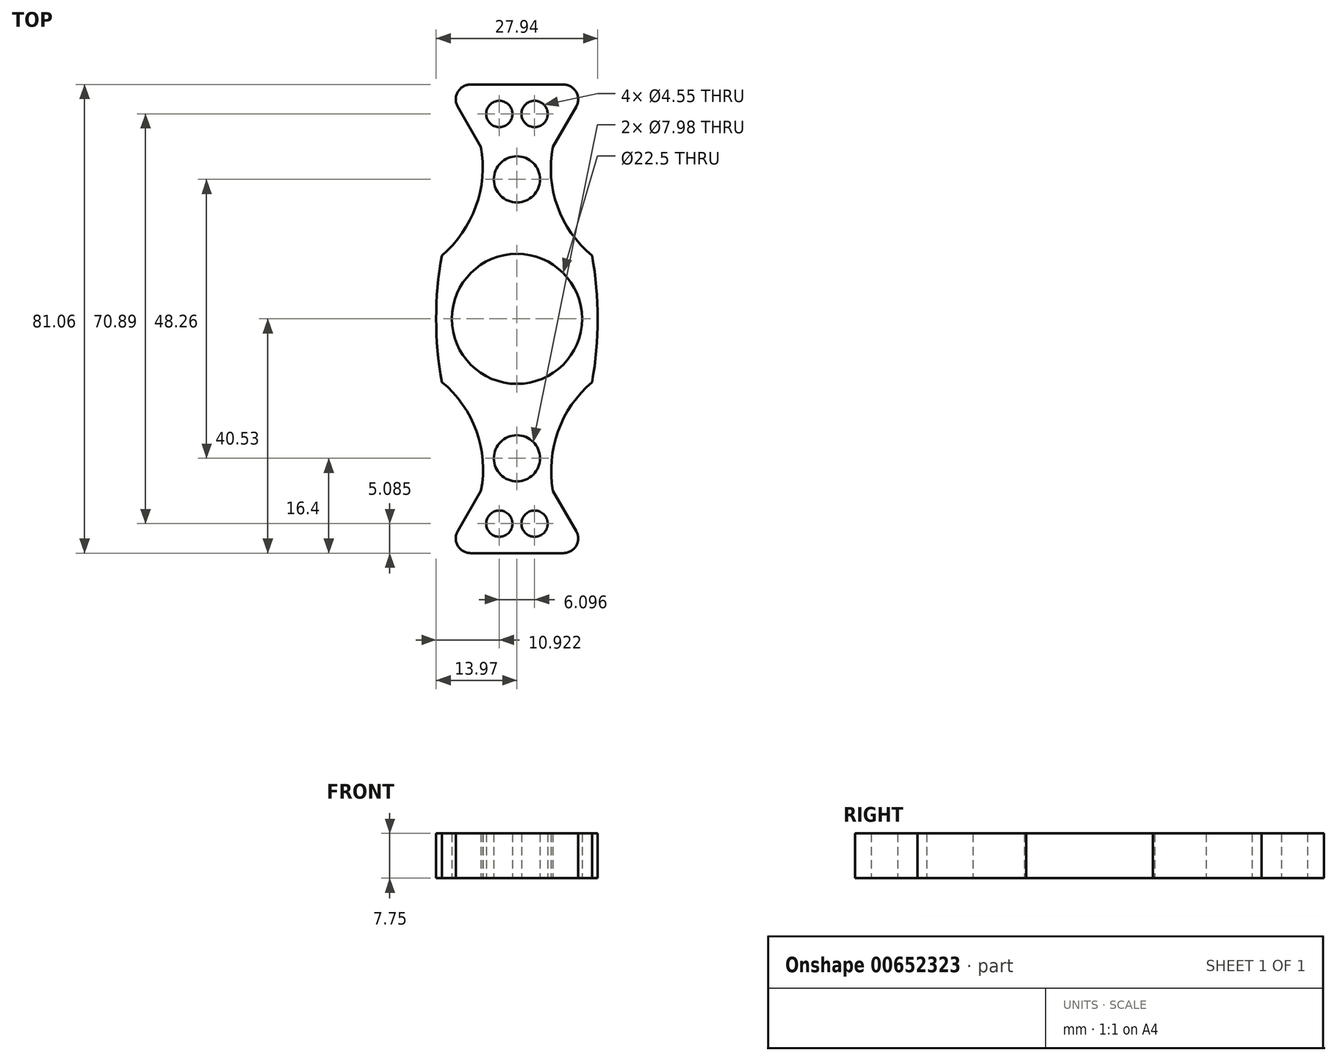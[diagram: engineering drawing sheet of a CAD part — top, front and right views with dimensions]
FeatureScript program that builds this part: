
annotation { "Feature Type Name" : "Feature", "Feature Type Description" : "" }
export const myFeature = defineFeature(function(context is Context, id is Id, definition is map)
    precondition{}
    {
        {
            var Q0;
            Q0=qCreatedBy(makeId("Top.planeOp"),FACE);
            var sketch = newSketch(context, id + "F0", { "sketchPlane" : qUnion([Q0])});
            skCircle(sketch, "E0", {"center": v(0, 0) * mm, "radius": 11.25 * mm});
            skLineSegment(sketch, "E1.0", {"start": v(-6.22, 29.76) * mm, "end": v(-10.24, 36.72) * mm});
            skLineSegment(sketch, "E1.1", {"start": v(-8.04, 40.53) * mm, "end": v(8.04, 40.53) * mm});
            skLineSegment(sketch, "E1.2", {"start": v(10.24, 36.72) * mm, "end": v(6.22, 29.76) * mm});
            skPoint(sketch, "E1.0.midPoint", {"position": v(-6.22, 29.76) * mm});
            skPoint(sketch, "E2.visualSharp", {"position": v(-12.44, 40.53) * mm});
            skArc(sketch, "E2.filletArc", {"start": v(-8.04, 40.53) * mm, "mid": v(-10.24, 39.26) * mm, "end": v(-10.24, 36.72) * mm});
            skPoint(sketch, "E3.visualSharp", {"position": v(12.44, 40.53) * mm});
            skArc(sketch, "E3.filletArc", {"start": v(10.24, 36.72) * mm, "mid": v(10.24, 39.26) * mm, "end": v(8.04, 40.53) * mm});
            skPoint(sketch, "E4.orphan", {"position": v(0, 18.99) * mm});
            skCircle(sketch, "E5", {"center": v(3.05, 35.45) * mm, "radius": 2.27 * mm});
            skCircle(sketch, "E6", {"center": v(-3.05, 35.45) * mm, "radius": 2.27 * mm});
            skLineSegment(sketch, "E7.1.1", {"start": v(-10.24, -36.72) * mm, "end": v(-6.22, -29.76) * mm});
            skArc(sketch, "E7.1.2", {"start": v(-10.24, -36.72) * mm, "mid": v(-10.24, -39.26) * mm, "end": v(-8.04, -40.53) * mm});
            skLineSegment(sketch, "E7.1.3", {"start": v(8.04, -40.53) * mm, "end": v(-8.04, -40.53) * mm});
            skArc(sketch, "E7.1.4", {"start": v(8.04, -40.53) * mm, "mid": v(10.24, -39.26) * mm, "end": v(10.24, -36.72) * mm});
            skLineSegment(sketch, "E7.1.5", {"start": v(6.22, -29.76) * mm, "end": v(10.24, -36.72) * mm});
            skCircle(sketch, "E7.1.10", {"center": v(-3.05, -35.45) * mm, "radius": 2.27 * mm});
            skCircle(sketch, "E7.1.11", {"center": v(3.05, -35.45) * mm, "radius": 2.27 * mm});
            skPoint(sketch, "E8.center.orphan", {"position": v(0, 16.59) * mm});
            skPoint(sketch, "E9.end.orphan", {"position": v(8.58, 10.94) * mm});
            skPoint(sketch, "E10.start.orphan", {"position": v(-8.58, 10.94) * mm});
            skArc(sketch, "E11", {"start": v(-12.98, 10.94) * mm, "mid": v(-13.97, 0) * mm, "end": v(-12.98, -10.94) * mm});
            skArc(sketch, "E12.1.0", {"start": v(12.98, -10.94) * mm, "mid": v(13.97, 0) * mm, "end": v(12.98, 10.94) * mm});
            skArc(sketch, "E13", {"start": v(6.22, 29.76) * mm, "mid": v(7, 19.42) * mm, "end": v(12.98, 10.94) * mm});
            skArc(sketch, "E14", {"start": v(-12.98, 10.94) * mm, "mid": v(-7.1, 19.45) * mm, "end": v(-6.22, 29.76) * mm});
            skArc(sketch, "E15.1.0", {"start": v(12.98, -10.94) * mm, "mid": v(7.1, -19.45) * mm, "end": v(6.22, -29.76) * mm});
            skArc(sketch, "E15.1.1", {"start": v(-6.22, -29.76) * mm, "mid": v(-7, -19.42) * mm, "end": v(-12.98, -10.94) * mm});
            skPoint(sketch, "E16.orphan", {"position": v(6.22, 29.76) * mm});
            skPoint(sketch, "E17.orphan", {"position": v(6.22, -29.76) * mm});
            skPoint(sketch, "E18.center.orphan", {"position": v(0, 29.84) * mm});
            skPoint(sketch, "E1.cCircle.center.orphan", {"position": v(0, 33.35) * mm});
            skPoint(sketch, "E19.center.orphan", {"position": v(0, 24.13) * mm});
            skCircle(sketch, "E20", {"center": v(0, 24.13) * mm, "radius": 4 * mm});
            skCircle(sketch, "E21.1.0", {"center": v(0, -24.13) * mm, "radius": 4 * mm});
            skSolve(sketch);
        }
        {
            var Q0;
            Q0 = qSketchRegion(id + "F0", true);
            extrude(context, id + "F1", {"entities" : qUnion([Q0]), "depth" : 7.75 * mm, "offsetDistance" : 25.4 * mm});
        }
    });
